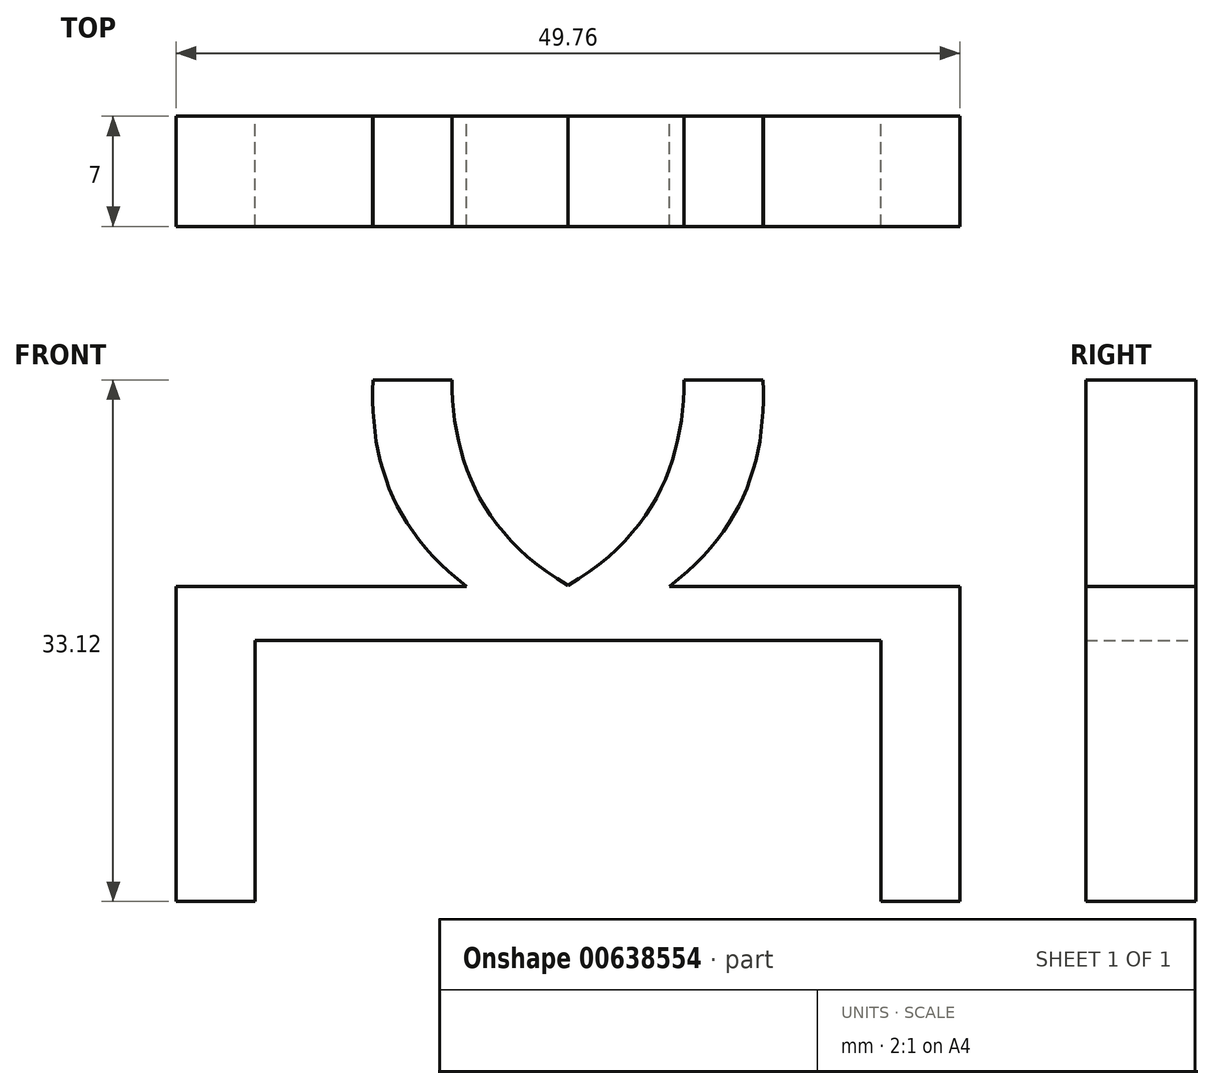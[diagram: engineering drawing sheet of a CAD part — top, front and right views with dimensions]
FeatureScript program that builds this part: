
annotation { "Feature Type Name" : "Feature", "Feature Type Description" : "" }
export const myFeature = defineFeature(function(context is Context, id is Id, definition is map)
    precondition{}
    {
        {
            var Q0;
            Q0=qCreatedBy(makeId("Front.planeOp"),FACE);
            var sketch = newSketch(context, id + "F0", { "sketchPlane" : qUnion([Q0])});
            skLineSegment(sketch, "E0", {"start": v(0.12, -1.72) * mm, "end": v(-24.88, -1.72) * mm});
            skLineSegment(sketch, "E1", {"start": v(-24.88, 1.72) * mm, "end": v(-24.88, -1.72) * mm});
            skLineSegment(sketch, "E2", {"start": v(-24.88, 1.72) * mm, "end": v(0.12, 1.72) * mm});
            skLineSegment(sketch, "E3.MirrorCS", {"start": v(-0.12, -1.72) * mm, "end": v(24.88, -1.72) * mm});
            skLineSegment(sketch, "E4.MirrorCS", {"start": v(24.88, 1.72) * mm, "end": v(24.88, -1.72) * mm});
            skLineSegment(sketch, "E5.MirrorCS", {"start": v(24.88, 1.72) * mm, "end": v(-0.12, 1.72) * mm});
            skLineSegment(sketch, "E6.top", {"start": v(-24.88, -18.28) * mm, "end": v(-19.88, -18.28) * mm});
            skLineSegment(sketch, "E6.left", {"start": v(-24.88, 1.72) * mm, "end": v(-24.88, -18.28) * mm});
            skLineSegment(sketch, "E6.right", {"start": v(-19.88, -2.13) * mm, "end": v(-19.88, -18.28) * mm});
            skLineSegment(sketch, "E7.MirrorCS", {"start": v(19.88, -2.13) * mm, "end": v(19.88, -18.28) * mm});
            skLineSegment(sketch, "E8.MirrorCS", {"start": v(24.88, 1.72) * mm, "end": v(24.88, -18.28) * mm});
            skLineSegment(sketch, "E9.MirrorCS", {"start": v(24.88, -18.28) * mm, "end": v(19.88, -18.28) * mm});
            skLineSegment(sketch, "E10", {"start": v(-19.88, -2.13) * mm, "end": v(-19.88, -1.72) * mm});
            skLineSegment(sketch, "E11", {"start": v(19.88, -2.13) * mm, "end": v(19.88, -1.72) * mm});
            skFitSpline(sketch, "E12", {"points": [v(0.12, 1.72) * mm, v(-7.37, 14.84) * mm], "startDerivative": vector(-16.86, 9.68) * mm, "endDerivative": vector(0, 15.12) * mm});
            skPoint(sketch, "E13.1.internal.snap0", {"position": v(-12.38, 1.72) * mm});
            skFitSpline(sketch, "E13", {"points": [v(-6.44, 1.72) * mm, v(-12.38, 14.84) * mm], "startDerivative": vector(-14, 10.8) * mm, "endDerivative": vector(0.64, 15.68) * mm});
            skLineSegment(sketch, "E14", {"start": v(-7.37, 14.84) * mm, "end": v(-12.38, 14.84) * mm});
            skFitSpline(sketch, "E15.MirrorCS", {"points": [v(-0.12, 1.72) * mm, v(7.37, 14.84) * mm], "startDerivative": vector(16.86, 9.68) * mm, "endDerivative": vector(0, 15.12) * mm});
            skLineSegment(sketch, "E16.MirrorCS", {"start": v(7.37, 14.84) * mm, "end": v(12.38, 14.84) * mm});
            skFitSpline(sketch, "E17.MirrorCS", {"points": [v(6.44, 1.72) * mm, v(12.38, 14.84) * mm], "startDerivative": vector(14, 10.8) * mm, "endDerivative": vector(-0.64, 15.68) * mm});
            skSolve(sketch);
        }
        {
            var Q0;
            Q0 = qSketchRegion(id + "F0", true);
            extrude(context, id + "F1", {"entities" : qUnion([Q0]), "depth" : 7 * mm, "offsetDistance" : 25 * mm});
        }
    });
